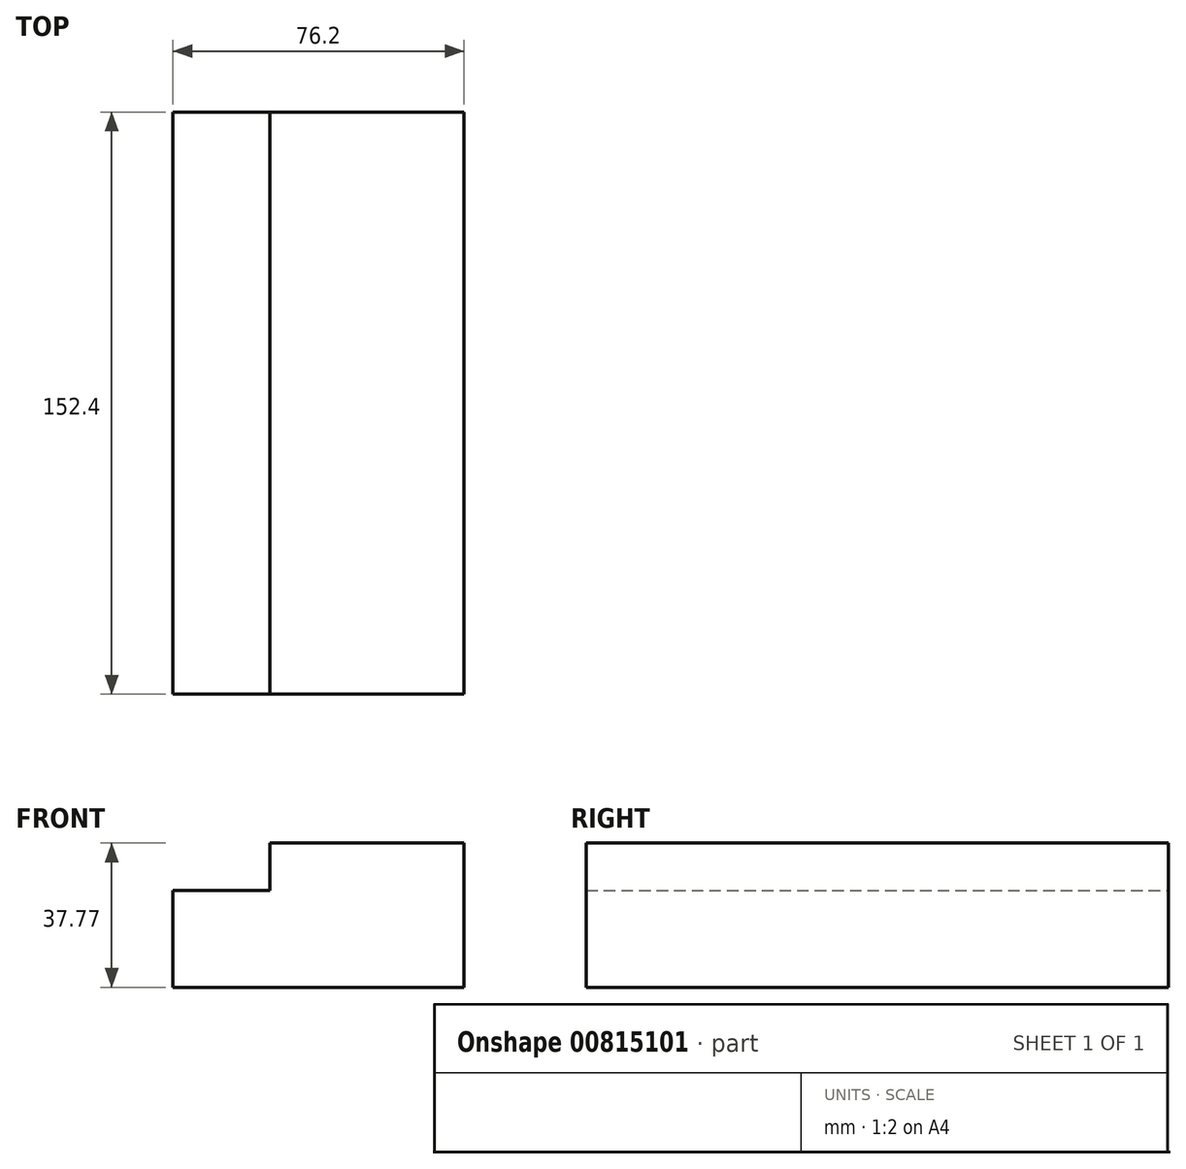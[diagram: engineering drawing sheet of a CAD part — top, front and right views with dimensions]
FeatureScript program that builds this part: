
annotation { "Feature Type Name" : "Feature", "Feature Type Description" : "" }
export const myFeature = defineFeature(function(context is Context, id is Id, definition is map)
    precondition{}
    {
        {
            var Q0;
            Q0=qCreatedBy(makeId("Front.planeOp"),FACE);
            var sketch = newSketch(context, id + "F0", { "sketchPlane" : qUnion([Q0])});
            skLineSegment(sketch, "E0", {"start": v(-76.2, 0) * mm, "end": v(-76.2, 25.4) * mm});
            skLineSegment(sketch, "E1", {"start": v(-76.2, 25.4) * mm, "end": v(-50.8, 25.4) * mm});
            skLineSegment(sketch, "E2", {"start": v(-50.8, 25.4) * mm, "end": v(-50.8, 37.77) * mm});
            skLineSegment(sketch, "E3", {"start": v(-50.8, 37.77) * mm, "end": v(0, 37.77) * mm});
            skLineSegment(sketch, "E4", {"start": v(0, 37.77) * mm, "end": v(0, 0) * mm});
            skLineSegment(sketch, "E5", {"start": v(0, 0) * mm, "end": v(-76.2, 0) * mm});
            skSolve(sketch);
        }
        {
            var Q0;
            Q0 = qSketchRegion(id + "F0", true);
            extrude(context, id + "F1", {"entities" : qUnion([Q0]), "depth" : 152.4 * mm, "offsetDistance" : 25.4 * mm});
        }
    });
